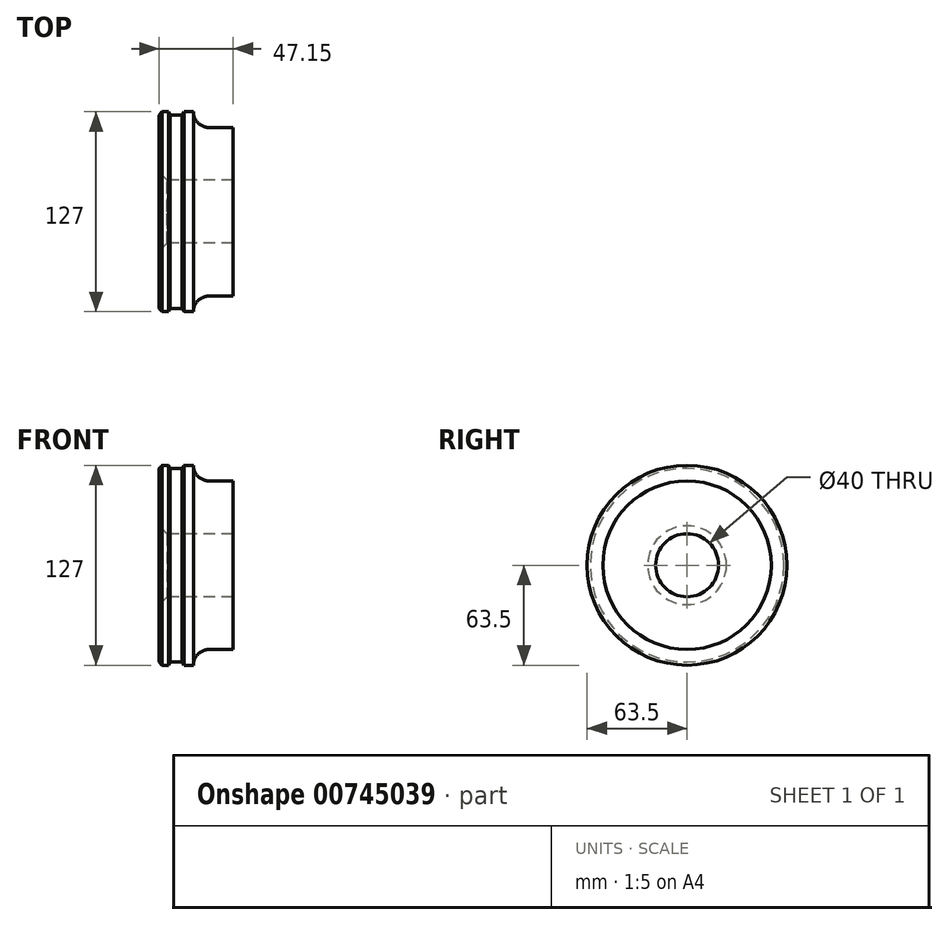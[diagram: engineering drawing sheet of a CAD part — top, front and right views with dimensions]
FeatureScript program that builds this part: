
annotation { "Feature Type Name" : "Feature", "Feature Type Description" : "" }
export const myFeature = defineFeature(function(context is Context, id is Id, definition is map)
    precondition{}
    {
        {
            var Q0;
            Q0=qCreatedBy(makeId("Front.planeOp"),FACE);
            var sketch = newSketch(context, id + "F0", { "sketchPlane" : qUnion([Q0])});
            skLineSegment(sketch, "E0", {"start": v(-228.27, 0) * mm, "end": v(214.38, 0) * mm});
            skLineSegment(sketch, "E1", {"start": v(-47.15, 0) * mm, "end": v(-47.15, 63.5) * mm});
            skLineSegment(sketch, "E2", {"start": v(-47.15, 63.5) * mm, "end": v(-41.15, 63.5) * mm});
            skLineSegment(sketch, "E3", {"start": v(-41.15, 63.5) * mm, "end": v(-40, 61.5) * mm});
            skLineSegment(sketch, "E4", {"start": v(-40, 61.5) * mm, "end": v(-32.5, 61.5) * mm});
            skLineSegment(sketch, "E5", {"start": v(-32.5, 61.5) * mm, "end": v(-31.35, 63.5) * mm});
            skLineSegment(sketch, "E6", {"start": v(-31.35, 63.5) * mm, "end": v(-25.35, 63.5) * mm});
            skLineSegment(sketch, "E7", {"start": v(-25.35, 63.5) * mm, "end": v(-25.35, 53.5) * mm});
            skLineSegment(sketch, "E8", {"start": v(-25.35, 53.5) * mm, "end": v(0, 53.5) * mm});
            skLineSegment(sketch, "E9", {"start": v(0, 53.5) * mm, "end": v(0, 0) * mm});
            skLineSegment(sketch, "E10", {"start": v(-47.15, 20) * mm, "end": v(0, 20) * mm});
            skSolve(sketch);
        }
        {
            var Q0;
            {var subQ0=sQuery(id+"F0.wireOp",EDGE,"E2");Q0=makeQuery(id+"F0.imprint","IMPRINT",FACE,{"disambiguationData":[TD([[makeQuery(id+"F0.imprint","IMPRINT",EDGE,{"derivedFrom":subQ0}),-1.0]])]});}
            var Q1;
            Q1=sQuery(id+"F0.wireOp",EDGE,"E0");
            revolve(context, id + "F1", {"surfaceOperationType" : NewSurfaceOperationType.NEW, "entities" : qUnion([Q0]), "axis" : qUnion([Q1]), "revolveType" : RevolveType.FULL});
        }
        {
            var Q0;
            Q0=makeQuery(id+"F1.opRevolve","SWEPT_EDGE",EDGE,{"disambiguationData":[OSD([sQuery(id+"F0.wireOp",EDGE,"E7"),sQuery(id+"F0.wireOp",EDGE,"E8")])]});
            fillet(context, id + "F2", {"entities" : qUnion([Q0]), "radius" : 10 * mm, "tangentPropagation" : true, "allowEdgeOverflow" : false});
        }
        {
            var Q0;
            Q0=makeQuery(id+"F1.opRevolve","SWEPT_EDGE",EDGE,{"disambiguationData":[OSD([sQuery(id+"F0.wireOp",EDGE,"E1"),sQuery(id+"F0.wireOp",EDGE,"E10")])]});
            var Q1;
            Q1=makeQuery(id+"F49NhLdHTOX9pwN_1.1.F1.opRevolve","SWEPT_EDGE",EDGE,{"disambiguationData":[OSD([sQuery(id+"F0.wireOp",EDGE,"E1"),sQuery(id+"F0.wireOp",EDGE,"E10")])]});
            chamfer(context, id + "F3", {"entities" : qUnion([Q0, Q1]), "width" : 5 * mm, "tangentPropagation" : true});
        }
        {
            var Q0;
            Q0=makeQuery(id+"F1.opRevolve","SWEPT_EDGE",EDGE,{"disambiguationData":[OSD([sQuery(id+"F0.wireOp",EDGE,"E1"),sQuery(id+"F0.wireOp",EDGE,"E2")])]});
            chamfer(context, id + "F4", {"entities" : qUnion([Q0]), "width" : 2 * mm, "tangentPropagation" : true});
        }
    });
